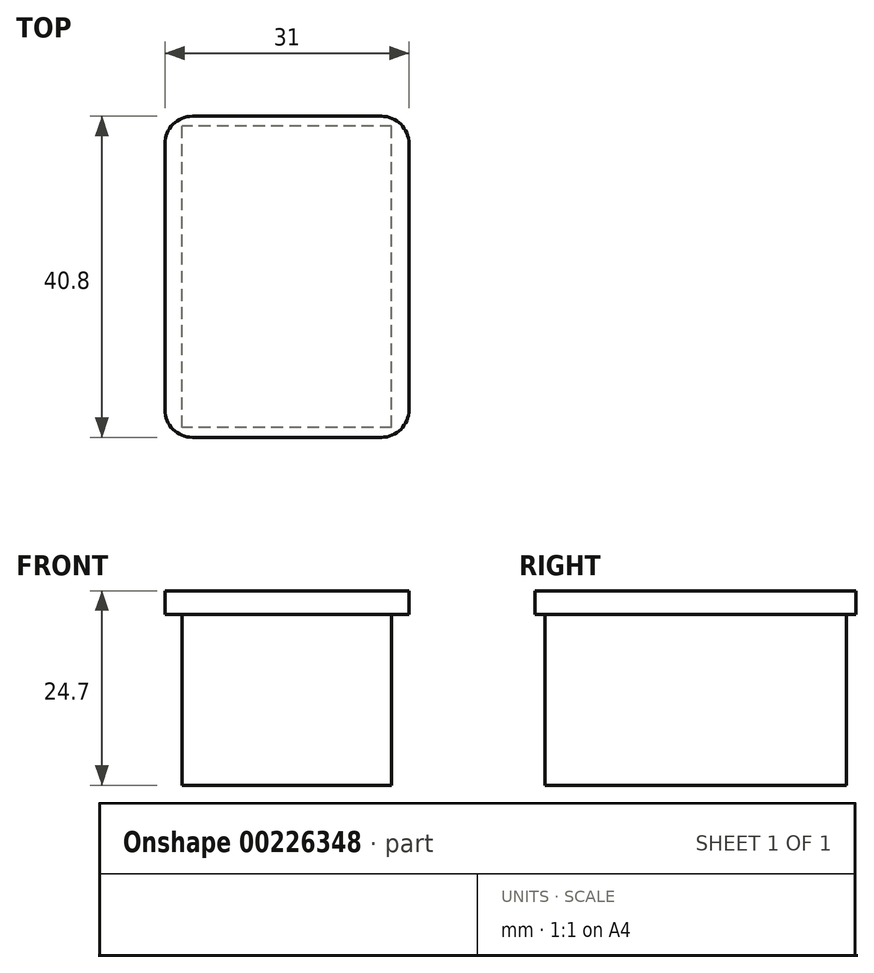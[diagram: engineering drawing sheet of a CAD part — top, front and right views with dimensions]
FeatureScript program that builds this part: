
annotation { "Feature Type Name" : "Feature", "Feature Type Description" : "" }
export const myFeature = defineFeature(function(context is Context, id is Id, definition is map)
    precondition{}
    {
        {
            var Q0;
            Q0=qCreatedBy(makeId("Top.planeOp"),FACE);
            var sketch = newSketch(context, id + "F0", { "sketchPlane" : qUnion([Q0])});
            skLineSegment(sketch, "E0.bottom", {"start": v(13.3, -19.15) * mm, "end": v(-13.3, -19.15) * mm});
            skLineSegment(sketch, "E0.top", {"start": v(13.3, 19.15) * mm, "end": v(-13.3, 19.15) * mm});
            skLineSegment(sketch, "E0.left", {"start": v(13.3, -19.15) * mm, "end": v(13.3, 19.15) * mm});
            skLineSegment(sketch, "E0.right", {"start": v(-13.3, -19.15) * mm, "end": v(-13.3, 19.15) * mm});
            skPoint(sketch, "E0.middle", {"position": v(0, 0) * mm});
            skSolve(sketch);
        }
        {
            var Q0;
            Q0 = qSketchRegion(id + "F0", true);
            extrude(context, id + "F1", {"entities" : qUnion([Q0]), "depth" : 21.7 * mm});
        }
        {
            var Q0;
            Q0=makeQuery(id+"F1.opExtrude","CAP_FACE",FACE,{"disambiguationData":[OSD([sQuery(id+"F0.wireOp",EDGE,"E0.bottom"),sQuery(id+"F0.wireOp",EDGE,"E0.top"),sQuery(id+"F0.wireOp",EDGE,"E0.left"),sQuery(id+"F0.wireOp",EDGE,"E0.right")])],"isStart":false});
            var sketch = newSketch(context, id + "F2", { "sketchPlane" : qUnion([Q0])});
            skLineSegment(sketch, "E1.bottom", {"start": v(-12, 20.4) * mm, "end": v(12, 20.4) * mm});
            skLineSegment(sketch, "E1.top", {"start": v(-12, -20.4) * mm, "end": v(12, -20.4) * mm});
            skLineSegment(sketch, "E1.left", {"start": v(-15.5, 16.9) * mm, "end": v(-15.5, -16.9) * mm});
            skLineSegment(sketch, "E1.right", {"start": v(15.5, 16.9) * mm, "end": v(15.5, -16.9) * mm});
            skPoint(sketch, "E1.middle", {"position": v(0, 0) * mm});
            skPoint(sketch, "E2.visualSharp", {"position": v(-15.5, 20.4) * mm});
            skArc(sketch, "E2.filletArc", {"start": v(-12, 20.4) * mm, "mid": v(-14.47, 19.37) * mm, "end": v(-15.5, 16.9) * mm});
            skPoint(sketch, "E3.visualSharp", {"position": v(15.5, 20.4) * mm});
            skArc(sketch, "E3.filletArc", {"start": v(15.5, 16.9) * mm, "mid": v(14.47, 19.37) * mm, "end": v(12, 20.4) * mm});
            skPoint(sketch, "E4.visualSharp", {"position": v(15.5, -20.4) * mm});
            skArc(sketch, "E4.filletArc", {"start": v(12, -20.4) * mm, "mid": v(14.47, -19.37) * mm, "end": v(15.5, -16.9) * mm});
            skPoint(sketch, "E5.visualSharp", {"position": v(-15.5, -20.4) * mm});
            skArc(sketch, "E5.filletArc", {"start": v(-15.5, -16.9) * mm, "mid": v(-14.47, -19.37) * mm, "end": v(-12, -20.4) * mm});
            skSolve(sketch);
        }
        {
            var Q0;
            Q0 = qSketchRegion(id + "F2", true);
            extrude(context, id + "F3", {"entities" : qUnion([Q0]), "operationType" : NewBodyOperationType.ADD, "depth" : 3 * mm});
        }
    });
